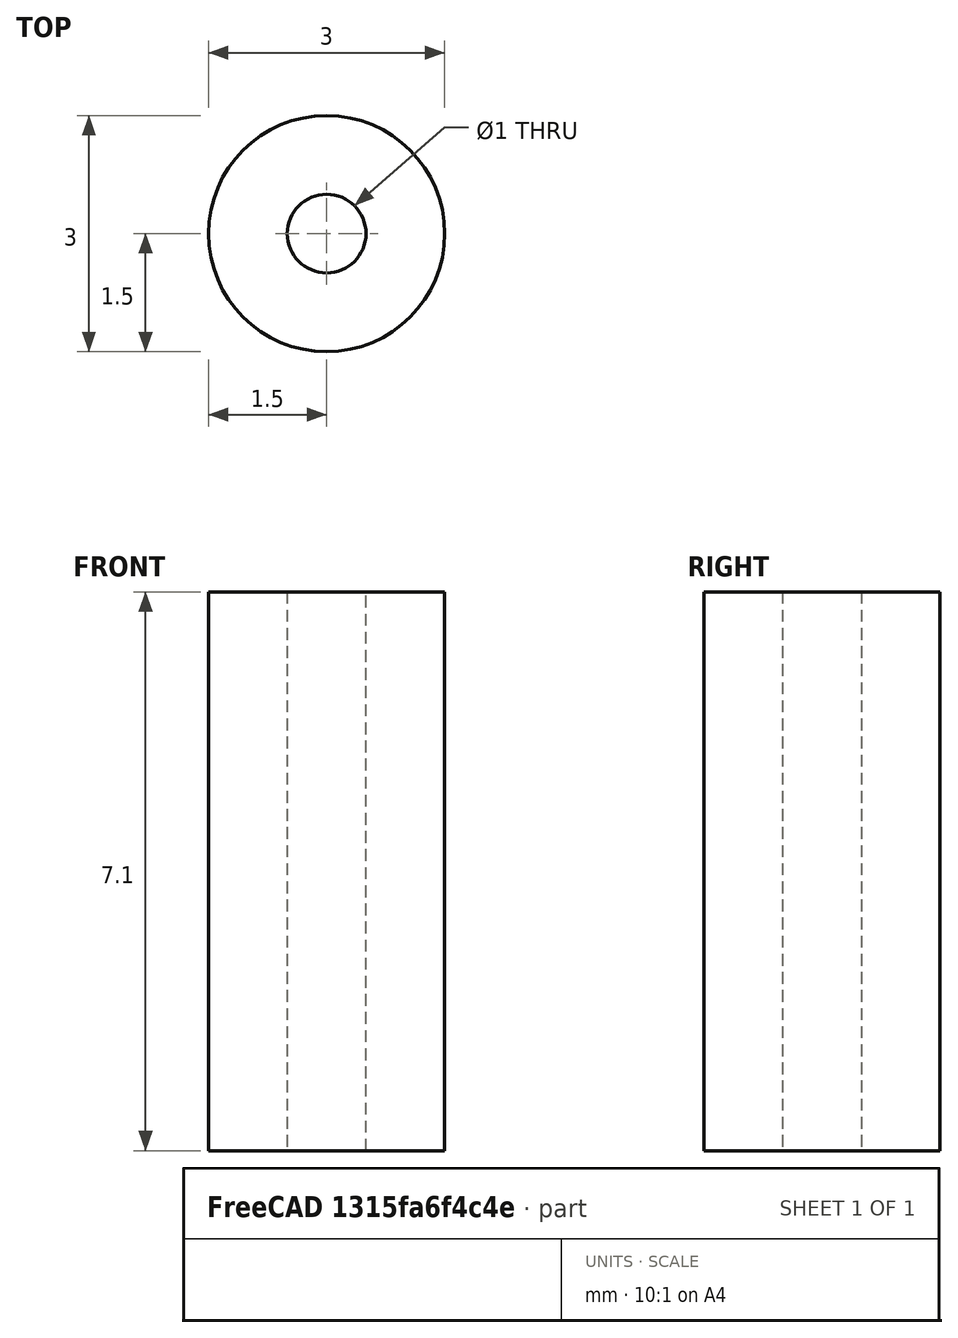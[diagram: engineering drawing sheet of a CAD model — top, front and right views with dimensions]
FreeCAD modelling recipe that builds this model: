
FCSTD DOCUMENT  (FreeCAD 0.19R24291 (Git))
Label: spring_stop_01
License: All rights reserved
LicenseURL: http://en.wikipedia.org/wiki/All_rights_reserved
objects: Spreadsheet::Sheet×1, Sketcher::SketchObject×1, PartDesign::Pad×1, PartDesign::Body×1
note: 4 computed .brp shape members not serialized (recipe doc carries the construction recipe); baked Part::Feature solids carry a one-line shape summary decoded from their .brp

FEATURE [Spreadsheet::Sheet] Spreadsheet
  cells = B2=spring ; C2=stop ; D2= washer; B4=wast h; C4(wast_h)=7.1; B5=wast r; C5(wast_r)=1.5; B6=rod r ; C6(hole_r)=0.5
FEATURE [Sketcher::SketchObject] Sketch
  FullyConstrained = true
  MapMode = 5
  Support = -> [XY_Plane]
  expr: Constraints[3] = Spreadsheet.hole_r
  expr: Constraints[2] = Spreadsheet.wast_r
  sketch-geometry (2):
    g0: Circle CenterX=0 CenterY=0 CenterZ=0 NormalX=0 NormalY=0 NormalZ=1 AngleXU=0 Radius=0.5
    g1: Circle CenterX=0 CenterY=0 CenterZ=0 NormalX=0 NormalY=0 NormalZ=1 AngleXU=0 Radius=1.5
  constraints (4):
    c: Coincident(g0,g-1)
    c: Coincident(g1,g0)
    c: Radius(g1) = 1.5
    c: Radius(g0) = 0.5
FEATURE [PartDesign::Pad] Pad
  Direction = (1,1,1)
  Length = 7.1
  Length2 = 100
  Profile = -> Sketch
  Type = 0
  expr: Length = Spreadsheet.wast_h
FEATURE [PartDesign::Body] Body
  Group = -> [Sketch,Pad]
  Origin = -> Origin
  Tip = -> Pad
